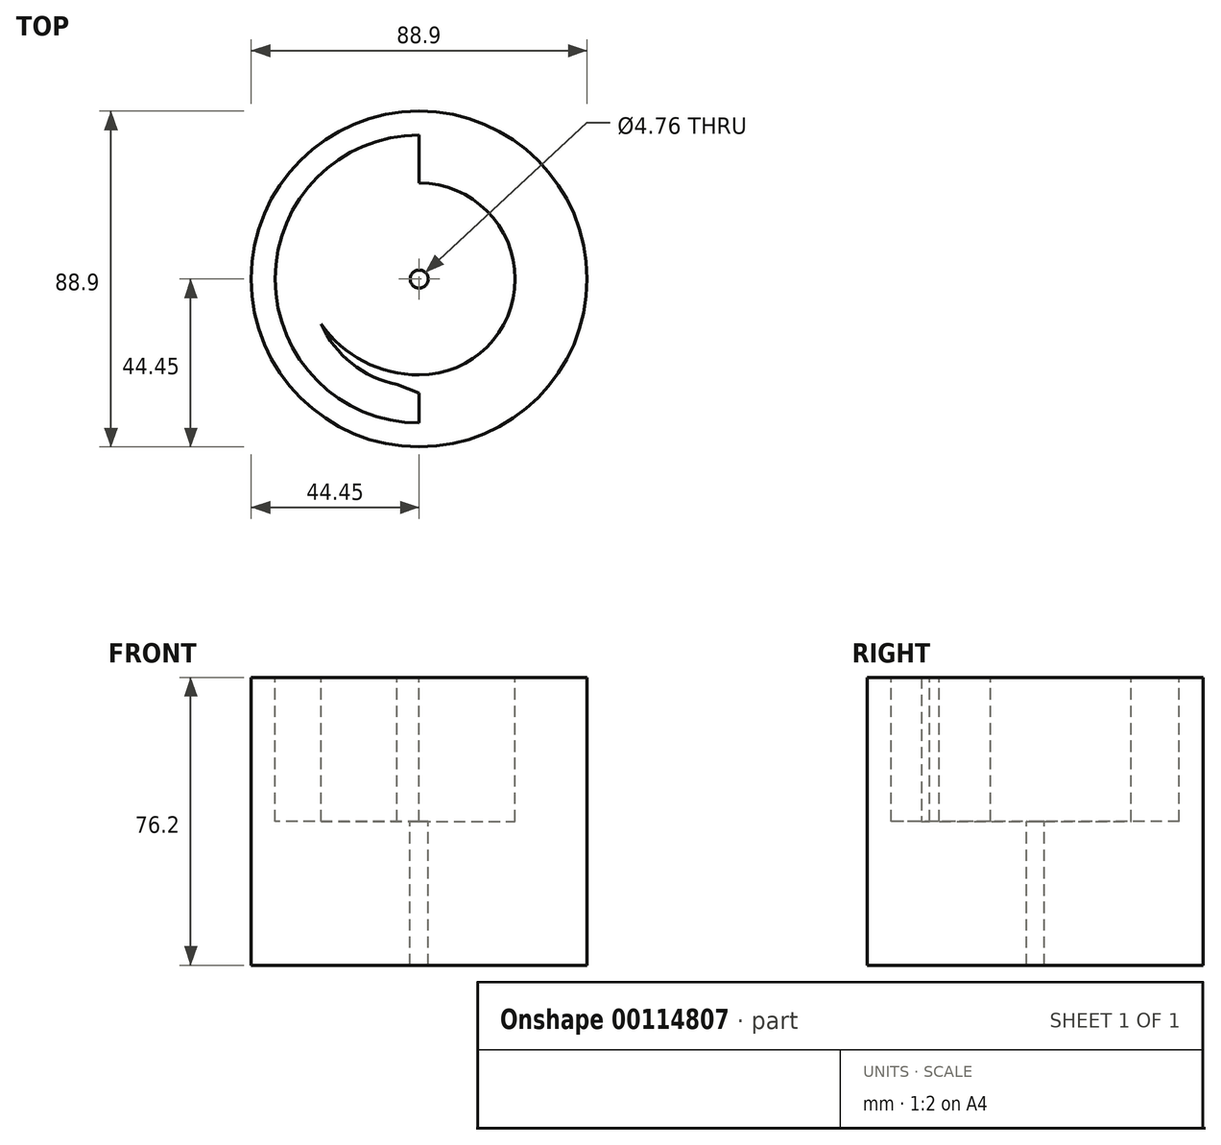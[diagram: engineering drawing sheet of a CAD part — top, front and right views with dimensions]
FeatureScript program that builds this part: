
annotation { "Feature Type Name" : "Feature", "Feature Type Description" : "" }
export const myFeature = defineFeature(function(context is Context, id is Id, definition is map)
    precondition{}
    {
        {
            var Q0;
            Q0=qCreatedBy(makeId("Top.planeOp"),FACE);
            var sketch = newSketch(context, id + "F0", { "sketchPlane" : qUnion([Q0])});
            skCircle(sketch, "E0", {"center": v(0, 0) * mm, "radius": 44.45 * mm});
            skSolve(sketch);
        }
        {
            var Q0;
            Q0 = qSketchRegion(id + "F0", true);
            extrude(context, id + "F1", {"entities" : qUnion([Q0]), "depth" : 76.2 * mm});
        }
        {
            var Q0;
            Q0=makeQuery(id+"F1.opExtrude","CAP_FACE",FACE,{"disambiguationData":[OSD([sQuery(id+"F0.wireOp",EDGE,"E0")])],"isStart":false});
            var sketch = newSketch(context, id + "F2", { "sketchPlane" : qUnion([Q0])});
            skCircle(sketch, "E1", {"center": v(0, 0) * mm, "radius": 38.1 * mm});
            skCircle(sketch, "E2", {"center": v(0, 0) * mm, "radius": 25.4 * mm});
            skCircle(sketch, "E3", {"center": v(0, 0) * mm, "radius": 28.58 * mm});
            skArc(sketch, "E4", {"start": v(0, 38.1) * mm, "mid": v(-31.75, 6.35) * mm, "end": v(0, -25.4) * mm});
            skLineSegment(sketch, "E5", {"start": v(0, 38.1) * mm, "end": v(0, -38.1) * mm});
            skLineSegment(sketch, "E6", {"start": v(28.58, 0) * mm, "end": v(38.1, 0) * mm});
            skCircle(sketch, "E7", {"center": v(0, 0) * mm, "radius": 2.38 * mm});
            skSolve(sketch);
        }
        {
            var Q0;
            {var subQ0=sQuery(id+"F2.wireOp",EDGE,"E4");var subQ1=sQuery(id+"F2.wireOp",EDGE,"E3");var subQ2=makeQuery(id+"F2.imprint","INTERSECT",VERTEX,{"derivedFrom":[subQ1,subQ0]});Q0=makeQuery(id+"F2.imprint","IMPRINT",FACE,{"disambiguationData":[TD([[makeQuery(id+"F2.imprint","IMPRINT",EDGE,{"disambiguationData":[TD([[subQ2,1.0]])],"derivedFrom":subQ1}),-1.0]])]});}
            var Q1;
            {var subQ1=sQuery(id+"F2.wireOp",EDGE,"E4");var subQ5=sQuery(id+"F2.wireOp",EDGE,"E3");var subQ6=makeQuery(id+"F2.imprint","INTERSECT",VERTEX,{"derivedFrom":[subQ5,subQ1]});Q1=makeQuery(id+"F2.imprint","IMPRINT",FACE,{"disambiguationData":[TD([[makeQuery(id+"F2.imprint","IMPRINT",EDGE,{"disambiguationData":[TD([[subQ6,1.0]])],"derivedFrom":subQ5}),1.0]])]});}
            var Q2;
            {var subQ0=sQuery(id+"F2.wireOp",EDGE,"E5");var subQ1=sQuery(id+"F2.wireOp",EDGE,"E2");var subQ3=makeQuery(id+"F2.imprint","INTERSECT",VERTEX,{"derivedFrom":[subQ1,subQ0]});Q2=makeQuery(id+"F2.imprint","IMPRINT",FACE,{"disambiguationData":[TD([[makeQuery(id+"F2.imprint","IMPRINT",EDGE,{"disambiguationData":[TD([[subQ3,-1.0]])],"derivedFrom":subQ1}),1.0]])]});}
            var Q3;
            {var subQ0=sQuery(id+"F2.wireOp",EDGE,"E5");var subQ1=sQuery(id+"F2.wireOp",EDGE,"E2");var subQ3=makeQuery(id+"F2.imprint","INTERSECT",VERTEX,{"derivedFrom":[subQ1,subQ0]});Q3=makeQuery(id+"F2.imprint","IMPRINT",FACE,{"disambiguationData":[TD([[makeQuery(id+"F2.imprint","IMPRINT",EDGE,{"disambiguationData":[TD([[subQ3,1.0]])],"derivedFrom":subQ1}),1.0]])]});}
            var Q4;
            {var subQ0=sQuery(id+"F2.wireOp",EDGE,"E5");var subQ4=sQuery(id+"F2.wireOp",EDGE,"E3");var subQ5=makeQuery(id+"F2.imprint","INTERSECT",VERTEX,{"disambiguationData":[OD(0.0)],"derivedFrom":[subQ4,subQ0]});Q4=makeQuery(id+"F2.imprint","IMPRINT",FACE,{"disambiguationData":[TD([[makeQuery(id+"F2.imprint","IMPRINT",EDGE,{"disambiguationData":[TD([[subQ5,1.0]])],"derivedFrom":subQ4}),-1.0]])]});}
            extrude(context, id + "F3", {"entities" : qUnion([Q0, Q1, Q2, Q3, Q4]), "operationType" : NewBodyOperationType.REMOVE, "oppositeDirection" : true, "depth" : 38.1 * mm});
        }
        {
            var Q0;
            Q0=makeQuery(id+"F3.boolean.opBoolean","COPY",EDGE,{"derivedFrom":makeQuery(id+"F3.opExtrude","SWEPT_EDGE",EDGE,{"disambiguationData":[OSD([sQuery(id+"F2.wireOp",EDGE,"E3"),sQuery(id+"F2.wireOp",EDGE,"E5")])]})});
            chamfer(context, id + "F4", {"entities" : qUnion([Q0]), "chamferType" : ChamferType.OFFSET_ANGLE, "width" : 6.35 * mm, "oppositeDirection" : false, "angle" : 20 * degree});
        }
        {
            var Q0;
            Q0=makeQuery(id+"F3.boolean.opBoolean","SPLIT",FACE,{"disambiguationData":[TD([makeQuery(id+"F3.opExtrude","SWEPT_FACE",FACE,{"disambiguationData":[OSD([sQuery(id+"F2.wireOp",EDGE,"E7")])]})])],"derivedFrom":makeQuery(id+"F1.opExtrude","CAP_FACE",FACE,{"disambiguationData":[OSD([sQuery(id+"F0.wireOp",EDGE,"E0")])],"isStart":false})});
            var Q1;
            Q1=sQuery(id+"F2.wireOp",EDGE,"E7");
            extrude(context, id + "F5", {"entities" : qUnion([Q0]), "operationType" : NewBodyOperationType.REMOVE, "surfaceEntities" : qUnion([Q1]), "endBound" : BoundingType.THROUGH_ALL, "oppositeDirection" : true, "depth" : 25.4 * mm});
        }
    });
